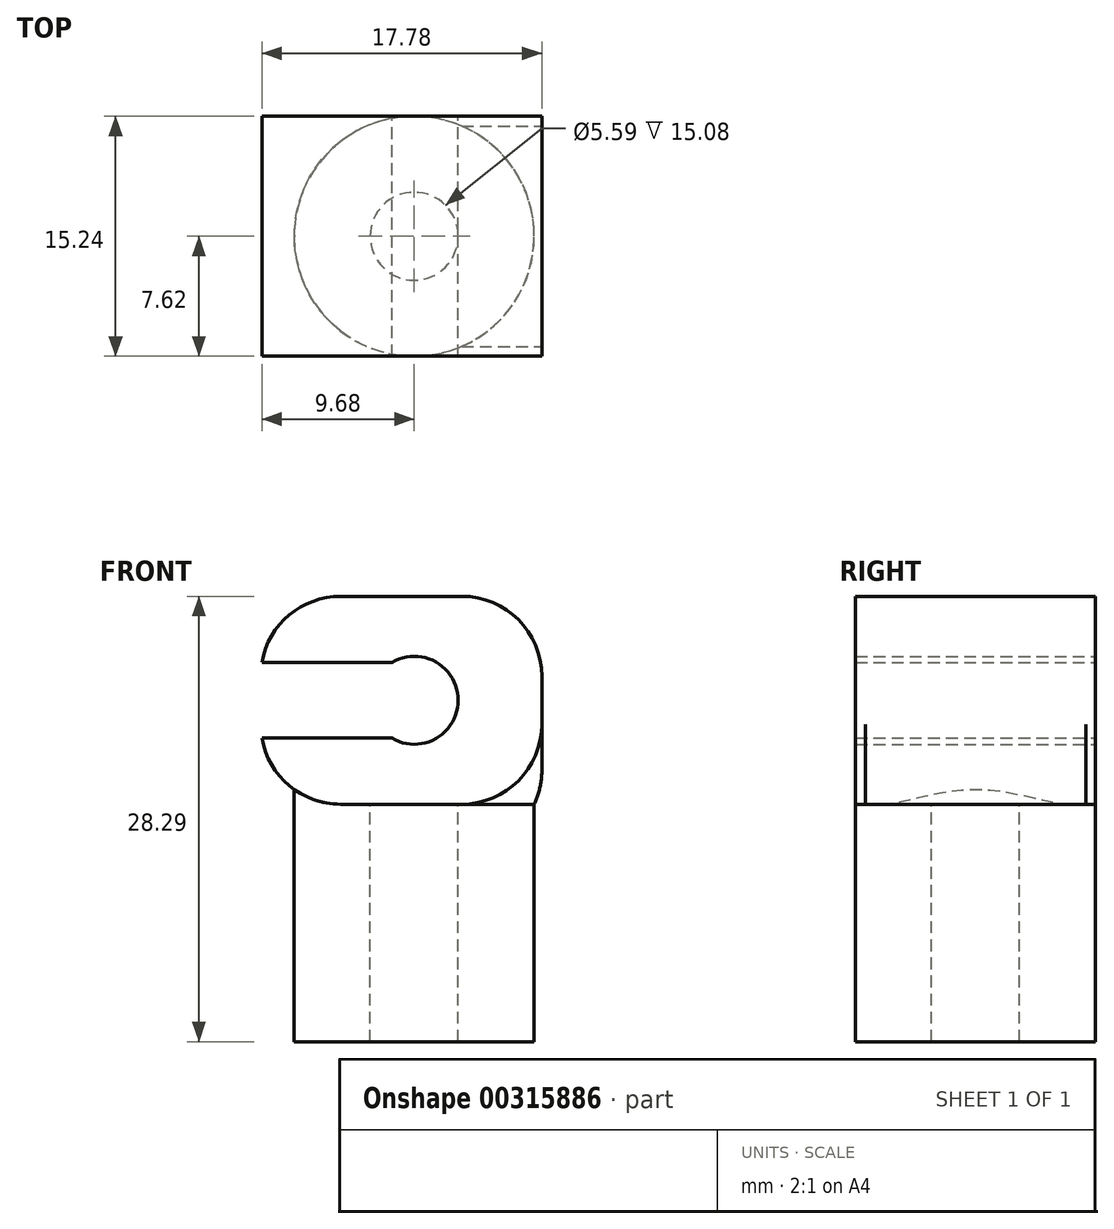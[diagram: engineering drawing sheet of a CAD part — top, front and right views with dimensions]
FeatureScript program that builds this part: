
annotation { "Feature Type Name" : "Feature", "Feature Type Description" : "" }
export const myFeature = defineFeature(function(context is Context, id is Id, definition is map)
    precondition{}
    {
        {
            var Q0;
            Q0=qCreatedBy(makeId("Top.planeOp"),FACE);
            var sketch = newSketch(context, id + "F0", { "sketchPlane" : qUnion([Q0])});
            skCircle(sketch, "E0", {"center": v(0, 0) * mm, "radius": 7.62 * mm});
            skSolve(sketch);
        }
        {
            var Q0;
            Q0=makeQuery(id+"F0.imprint","IMPRINT",FACE,{"disambiguationData":[TD([[makeQuery(id+"F0.imprint","IMPRINT",EDGE,{"derivedFrom":sQuery(id+"F0.wireOp",EDGE,"E0")}),1.0]])]});
            extrude(context, id + "F1", {"entities" : qUnion([Q0]), "depth" : 15.24 * mm});
        }
        {
            var Q0;
            Q0=makeQuery(id+"F1.opExtrude","CAP_FACE",FACE,{"disambiguationData":[OSD([sQuery(id+"F0.wireOp",EDGE,"E0")])],"isStart":false});
            var sketch = newSketch(context, id + "F2", { "sketchPlane" : qUnion([Q0])});
            skCircle(sketch, "E1", {"center": v(0, 0) * mm, "radius": 2.8 * mm});
            skSolve(sketch);
        }
        {
            var Q0;
            Q0=makeQuery(id+"F2.imprint","IMPRINT",FACE,{"disambiguationData":[TD([[makeQuery(id+"F2.imprint","IMPRINT",EDGE,{"derivedFrom":sQuery(id+"F2.wireOp",EDGE,"E1")}),1.0]])]});
            var Q1;
            Q1=makeQuery(id+"F1.opExtrude","CAP_FACE",FACE,{"disambiguationData":[OSD([sQuery(id+"F0.wireOp",EDGE,"E0")])],"isStart":false});
            extrude(context, id + "F3", {"entities" : qUnion([Q0]), "operationType" : NewBodyOperationType.REMOVE, "endBound" : BoundingType.THROUGH_ALL, "oppositeDirection" : true, "endBoundEntityFace" : qUnion([Q1]), "depth" : 25.4 * mm});
        }
        {
            var Q0;
            Q0=qCreatedBy(makeId("Front.planeOp"),FACE);
            var sketch = newSketch(context, id + "F4", { "sketchPlane" : qUnion([Q0])});
            skLineSegment(sketch, "E2.bottom", {"start": v(-9.68, 15.08) * mm, "end": v(8.1, 15.08) * mm});
            skLineSegment(sketch, "E2.top", {"start": v(-9.68, 28.29) * mm, "end": v(8.1, 28.29) * mm});
            skLineSegment(sketch, "E2.left", {"start": v(-9.68, 15.08) * mm, "end": v(-9.68, 28.29) * mm});
            skLineSegment(sketch, "E2.right", {"start": v(8.1, 15.08) * mm, "end": v(8.1, 28.29) * mm});
            skSolve(sketch);
        }
        {
            var Q0;
            Q0 = qSketchRegion(id + "F4", true);
            extrude(context, id + "F5", {"entities" : qUnion([Q0]), "operationType" : NewBodyOperationType.ADD, "endBound" : BoundingType.SYMMETRIC, "depth" : 15.24 * mm});
        }
        {
            var Q0;
            Q0=makeQuery(id+"F5.opExtrude","CAP_FACE",FACE,{"disambiguationData":[OSD([sQuery(id+"F4.wireOp",EDGE,"E2.bottom"),sQuery(id+"F4.wireOp",EDGE,"E2.top"),sQuery(id+"F4.wireOp",EDGE,"E2.left"),sQuery(id+"F4.wireOp",EDGE,"E2.right")])],"isStart":true});
            var sketch = newSketch(context, id + "F6", { "sketchPlane" : qUnion([Q0])});
            skCircle(sketch, "E3", {"center": v(0, 21.68) * mm, "radius": 2.8 * mm});
            skPoint(sketch, "E3.centerSnap0", {"position": v(-8.1, 21.68) * mm});
            skLineSegment(sketch, "E4", {"start": v(9.68, 19.28) * mm, "end": v(1.42, 19.28) * mm});
            skLineSegment(sketch, "E5", {"start": v(9.68, 24.09) * mm, "end": v(1.42, 24.09) * mm});
            skSolve(sketch);
        }
        {
            var Q0;
            {var subQ0=sQuery(id+"F6.wireOp",EDGE,"E4");Q0=makeQuery(id+"F6.imprint","IMPRINT",FACE,{"disambiguationData":[TD([[makeQuery(id+"F6.imprint","IMPRINT",EDGE,{"derivedFrom":subQ0}),-1.0]])]});}
            var Q1;
            {var subQ0=sQuery(id+"F6.wireOp",EDGE,"E3");var subQ1=makeQuery(id+"F6.imprint","INTERSECT",VERTEX,{"derivedFrom":[subQ0,sQuery(id+"F6.wireOp",EDGE,"E4")]});Q1=makeQuery(id+"F6.imprint","IMPRINT",FACE,{"disambiguationData":[TD([[makeQuery(id+"F6.imprint","IMPRINT",EDGE,{"disambiguationData":[TD([[subQ1,1.0]])],"derivedFrom":subQ0}),1.0]])]});}
            extrude(context, id + "F7", {"entities" : qUnion([Q0, Q1]), "operationType" : NewBodyOperationType.REMOVE, "oppositeDirection" : true, "depth" : 25.4 * mm});
        }
        {
            var Q0;
            Q0=makeQuery(id+"F5.opExtrude","SWEPT_EDGE",EDGE,{"disambiguationData":[OSD([sQuery(id+"F4.wireOp",EDGE,"E2.bottom"),sQuery(id+"F4.wireOp",EDGE,"E2.right")])]});
            var Q1;
            Q1=makeQuery(id+"F5.opExtrude","SWEPT_EDGE",EDGE,{"disambiguationData":[OSD([sQuery(id+"F4.wireOp",EDGE,"E2.top"),sQuery(id+"F4.wireOp",EDGE,"E2.right")])]});
            var Q2;
            Q2=makeQuery(id+"F5.opExtrude","SWEPT_EDGE",EDGE,{"disambiguationData":[OSD([sQuery(id+"F4.wireOp",EDGE,"E2.top"),sQuery(id+"F4.wireOp",EDGE,"E2.left")])]});
            var Q3;
            Q3=makeQuery(id+"F5.opExtrude","SWEPT_EDGE",EDGE,{"disambiguationData":[OSD([sQuery(id+"F4.wireOp",EDGE,"E2.bottom"),sQuery(id+"F4.wireOp",EDGE,"E2.left")])]});
            fillet(context, id + "F8", {"entities" : qUnion([Q0, Q1, Q2, Q3]), "radius" : 5.08 * mm, "tangentPropagation" : true, "allowEdgeOverflow" : false});
        }
    });
